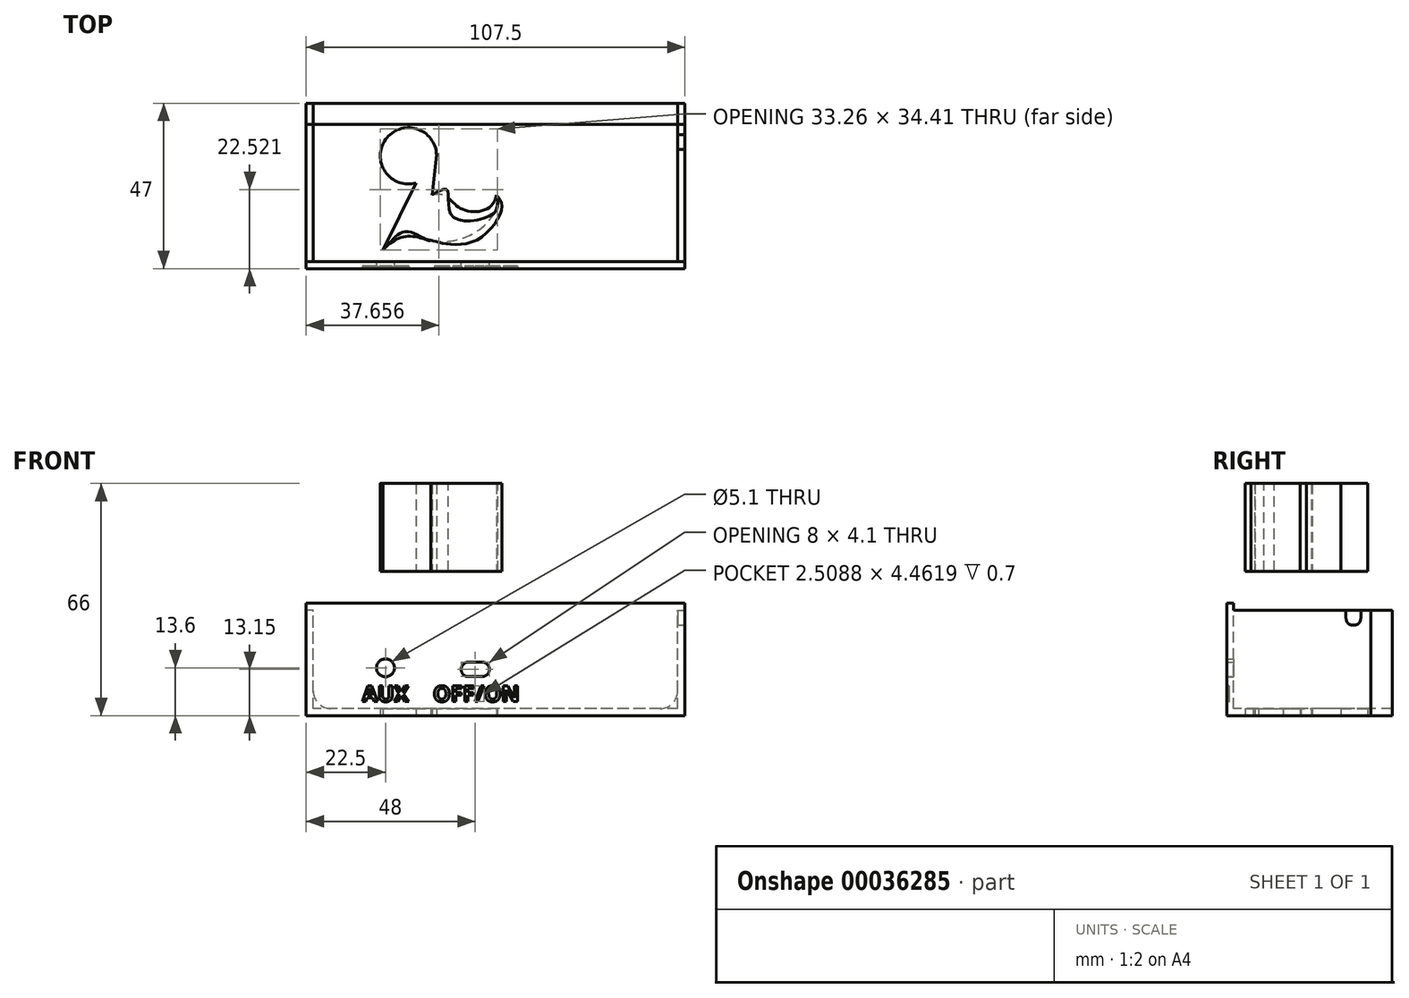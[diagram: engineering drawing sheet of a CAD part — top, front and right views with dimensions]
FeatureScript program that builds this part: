
annotation { "Feature Type Name" : "Feature", "Feature Type Description" : "" }
export const myFeature = defineFeature(function(context is Context, id is Id, definition is map)
    precondition{}
    {
        {
            var Q0;
            Q0=qCreatedBy(makeId("Top.planeOp"),FACE);
            var sketch = newSketch(context, id + "F0", { "sketchPlane" : qUnion([Q0])});
            skLineSegment(sketch, "E0.bottom", {"start": v(107.5, -32) * mm, "end": v(0, -32) * mm});
            skLineSegment(sketch, "E0.top", {"start": v(107.5, 0) * mm, "end": v(0, 0) * mm});
            skLineSegment(sketch, "E0.left", {"start": v(107.5, -32) * mm, "end": v(107.5, 0) * mm});
            skLineSegment(sketch, "E1", {"start": v(0, -32) * mm, "end": v(0, 0) * mm});
            skPoint(sketch, "E0.right.end.orphan", {"position": v(-106.05, 0) * mm});
            skSolve(sketch);
        }
        {
            var Q0;
            Q0=makeQuery(id+"F0.imprint","IMPRINT",FACE,{"disambiguationData":[TD([[makeQuery(id+"F0.imprint","IMPRINT",EDGE,{"derivedFrom":sQuery(id+"F0.wireOp",EDGE,"E0.bottom")}),-1.0]])]});
            extrude(context, id + "F1", {"entities" : qUnion([Q0]), "oppositeDirection" : true, "depth" : 2 * mm});
        }
        {
            var Q0;
            Q0=makeQuery(id+"F1.opExtrude","CAP_FACE",FACE,{"disambiguationData":[OSD([sQuery(id+"F0.wireOp",EDGE,"E0.bottom"),sQuery(id+"F0.wireOp",EDGE,"E0.top"),sQuery(id+"F0.wireOp",EDGE,"E0.left"),sQuery(id+"F0.wireOp",EDGE,"E1")])],"isStart":false});
            var sketch = newSketch(context, id + "F2", { "sketchPlane" : qUnion([Q0])});
            skLineSegment(sketch, "E2.0", {"start": v(105.5, 30) * mm, "end": v(2, 30) * mm});
            skLineSegment(sketch, "E2.1", {"start": v(105.5, 30) * mm, "end": v(105.5, 2) * mm});
            skLineSegment(sketch, "E2.2", {"start": v(105.5, 2) * mm, "end": v(2, 2) * mm});
            skLineSegment(sketch, "E2.3", {"start": v(2, 30) * mm, "end": v(2, 2) * mm});
            skLineSegment(sketch, "E3", {"start": v(2, 2) * mm, "end": v(0, 2) * mm});
            skLineSegment(sketch, "E4", {"start": v(105.5, 2) * mm, "end": v(107.5, 2) * mm});
            skSolve(sketch);
        }
        {
            var Q0;
            Q0=makeQuery(id+"F2.imprint","IMPRINT",FACE,{"disambiguationData":[TD([[makeQuery(id+"F2.imprint","IMPRINT",EDGE,{"derivedFrom":sQuery(id+"F2.wireOp",EDGE,"E2.0")}),-1.0]])]});
            extrude(context, id + "F3", {"entities" : qUnion([Q0]), "operationType" : NewBodyOperationType.ADD, "depth" : 39 * mm});
        }
        {
            var Q0;
            {var subQ0=sQuery(id+"F0.wireOp",EDGE,"E0.bottom");Q0=makeQuery(id+"F3.boolean.opBoolean","MERGE",FACE,{"derivedFrom":[makeQuery(id+"F1.opExtrude","SWEPT_FACE",FACE,{"disambiguationData":[OSD([subQ0])]}),makeQuery(id+"F3.opExtrude","SWEPT_FACE",FACE,{"disambiguationData":[OSD([subQ0])]})]});}
            var sketch = newSketch(context, id + "F4", { "sketchPlane" : qUnion([Q0])});
            skArc(sketch, "E5", {"start": v(31.19, -24.36) * mm, "mid": v(22.54, -36.75) * mm, "end": v(37.02, -32.4) * mm});
            skLineSegment(sketch, "E6", {"start": v(35.74, -20.94) * mm, "end": v(37.02, -32.4) * mm});
            skLineSegment(sketch, "E7", {"start": v(31.19, -24.36) * mm, "end": v(21.74, -5.32) * mm});
            skFitSpline(sketch, "E8", {"points": [v(35.39, -8.1) * mm, v(48.03, -10.36) * mm, v(54, -20.94) * mm], "startDerivative": vector(20.74, 5.18) * mm, "endDerivative": vector(-9.53, -21.5) * mm});
            skFitSpline(sketch, "E9", {"points": [v(21.74, -5.32) * mm, v(29.02, -9.2) * mm, v(35.39, -8.1) * mm], "startDerivative": vector(11.68, -12.14) * mm, "endDerivative": vector(6.82, 0.29) * mm});
            skFitSpline(sketch, "E10", {"points": [v(35.74, -20.94) * mm, v(43.74, -17.18) * mm, v(54, -20.94) * mm], "startDerivative": vector(27.47, -8.8) * mm, "endDerivative": vector(3.96, -29.24) * mm});
            skSolve(sketch);
        }
        {
            var Q0;
            Q0=qSketchRegion(id+"F4",true);
            extrude(context, id + "F5", {"entities" : qUnion([Q0]), "operationType" : NewBodyOperationType.REMOVE, "endBound" : BoundingType.THROUGH_ALL, "oppositeDirection" : true, "depth" : 25 * mm});
        }
        {
            var Q0;
            Q0=makeQuery(id+"F1.opExtrude","SWEPT_BODY",BODY,{"disambiguationData":[OSD([sQuery(id+"F0.wireOp",EDGE,"E0.bottom"),sQuery(id+"F0.wireOp",EDGE,"E0.top"),sQuery(id+"F0.wireOp",EDGE,"E0.left"),sQuery(id+"F0.wireOp",EDGE,"E1")])]});
            var Q1;
            Q1=makeQuery(id+"F3.opExtrude","CAP_EDGE",EDGE,{"disambiguationData":[OSD([sQuery(id+"F0.wireOp",EDGE,"E0.bottom")])],"isStart":false});
            transform(context, id + "F6", {"entities" : qUnion([Q0]), "transformType" : TransformType.ROTATION, "transformAxis" : qUnion([Q1]), "angle" : 90 * degree, "oppositeDirection" : true, "makeCopy" : false});
        }
        {
            var Q0;
            Q0=makeQuery(id+"F3.opExtrude","CAP_FACE",FACE,{"disambiguationData":[OSD([sQuery(id+"F0.wireOp",EDGE,"E0.bottom"),sQuery(id+"F0.wireOp",EDGE,"E0.left"),sQuery(id+"F0.wireOp",EDGE,"E1"),sQuery(id+"F2.wireOp",EDGE,"E2.0"),sQuery(id+"F2.wireOp",EDGE,"E2.1"),sQuery(id+"F2.wireOp",EDGE,"E2.3"),sQuery(id+"F2.wireOp",EDGE,"E3"),sQuery(id+"F2.wireOp",EDGE,"E4")])],"isStart":false});
            extrude(context, id + "F7", {"entities" : qUnion([Q0]), "depth" : 6 * mm});
        }
        {
            var Q0;
            Q0=makeQuery(id+"F3.opExtrude","CAP_EDGE",EDGE,{"disambiguationData":[OSD([sQuery(id+"F2.wireOp",EDGE,"E2.0")])],"isStart":true});
            var Q1;
            Q1=makeQuery(id+"F3.opExtrude","SWEPT_EDGE",EDGE,{"disambiguationData":[OSD([sQuery(id+"F2.wireOp",EDGE,"E2.0"),sQuery(id+"F2.wireOp",EDGE,"E2.3")])]});
            var Q2;
            Q2=makeQuery(id+"F3.opExtrude","SWEPT_EDGE",EDGE,{"disambiguationData":[OSD([sQuery(id+"F2.wireOp",EDGE,"E2.0"),sQuery(id+"F2.wireOp",EDGE,"E2.1")])]});
            fillet(context, id + "F8", {"entities" : qUnion([Q0, Q1, Q2]), "radius" : 5 * mm, "tangentPropagation" : true, "allowEdgeOverflow" : false});
        }
        {
            var Q0;
            Q0=makeQuery(id+"F1.opExtrude","CAP_FACE",FACE,{"disambiguationData":[OSD([sQuery(id+"F0.wireOp",EDGE,"E0.bottom"),sQuery(id+"F0.wireOp",EDGE,"E0.top"),sQuery(id+"F0.wireOp",EDGE,"E0.left"),sQuery(id+"F0.wireOp",EDGE,"E1")])],"isStart":false});
            var sketch = newSketch(context, id + "F9", { "sketchPlane" : qUnion([Q0])});
            skCircle(sketch, "E11", {"center": v(-22.5, -27.4) * mm, "radius": 2.55 * mm});
            skLineSegment(sketch, "E12.bottom", {"start": v(-46, -29.9) * mm, "end": v(-50, -29.9) * mm});
            skLineSegment(sketch, "E12.top", {"start": v(-46, -25.8) * mm, "end": v(-50, -25.8) * mm});
            skLineSegment(sketch, "E12.left", {"start": v(-44, -27.9) * mm, "end": v(-44, -27.8) * mm});
            skLineSegment(sketch, "E12.right", {"start": v(-52, -27.9) * mm, "end": v(-52, -27.8) * mm});
            skPoint(sketch, "E13.visualSharp", {"position": v(-44, -25.8) * mm});
            skArc(sketch, "E13.filletArc", {"start": v(-44, -27.8) * mm, "mid": v(-44.59, -26.39) * mm, "end": v(-46, -25.8) * mm});
            skPoint(sketch, "E14.visualSharp", {"position": v(-44, -29.9) * mm});
            skArc(sketch, "E14.filletArc", {"start": v(-46, -29.9) * mm, "mid": v(-44.59, -29.31) * mm, "end": v(-44, -27.9) * mm});
            skPoint(sketch, "E15.visualSharp", {"position": v(-52, -29.9) * mm});
            skArc(sketch, "E15.filletArc", {"start": v(-52, -27.9) * mm, "mid": v(-51.41, -29.31) * mm, "end": v(-50, -29.9) * mm});
            skPoint(sketch, "E16.visualSharp", {"position": v(-52, -25.8) * mm});
            skArc(sketch, "E16.filletArc", {"start": v(-50, -25.8) * mm, "mid": v(-51.41, -26.39) * mm, "end": v(-52, -27.8) * mm});
            skLineSegment(sketch, "E17", {"start": v(-48, -29.9) * mm, "end": v(-48, -25.8) * mm, "construction": true});
            skLineSegment(sketch, "E18", {"start": v(-48, -29.9) * mm, "end": v(-48, -32.37) * mm});
            skSolve(sketch);
        }
        {
            var Q0;
            Q0=makeQuery(id+"F9.imprint","IMPRINT",FACE,{"disambiguationData":[TD([[makeQuery(id+"F9.imprint","IMPRINT",EDGE,{"derivedFrom":sQuery(id+"F9.wireOp",EDGE,"E12.bottom")}),-1.0]])]});
            var Q1;
            Q1=makeQuery(id+"F9.imprint","IMPRINT",FACE,{"disambiguationData":[TD([[makeQuery(id+"F9.imprint","IMPRINT",EDGE,{"derivedFrom":sQuery(id+"F9.wireOp",EDGE,"E11")}),1.0]])]});
            extrude(context, id + "F10", {"entities" : qUnion([Q0, Q1]), "operationType" : NewBodyOperationType.REMOVE, "endBound" : BoundingType.THROUGH_ALL, "oppositeDirection" : true, "depth" : 25 * mm});
        }
        {
            var Q0;
            Q0=makeQuery(id+"F1.opExtrude","CAP_FACE",FACE,{"disambiguationData":[OSD([sQuery(id+"F0.wireOp",EDGE,"E0.bottom"),sQuery(id+"F0.wireOp",EDGE,"E0.top"),sQuery(id+"F0.wireOp",EDGE,"E0.left"),sQuery(id+"F0.wireOp",EDGE,"E1")])],"isStart":true});
            var sketch = newSketch(context, id + "F11", { "sketchPlane" : qUnion([Q0])});
            skLineSegment(sketch, "E19", {"start": v(22.5, -27.4) * mm, "end": v(22.5, -41) * mm, "construction": true});
            skLineSegment(sketch, "E20", {"start": v(22.5, -41) * mm, "end": v(32.53, -41) * mm, "construction": true});
            skSolve(sketch);
        }
        {
            var Q0;
            {var subQ0=sQuery(id+"F0.wireOp",EDGE,"E0.bottom");Q0=makeQuery(id+"F3.boolean.opBoolean","MERGE",FACE,{"derivedFrom":[makeQuery(id+"F1.opExtrude","SWEPT_FACE",FACE,{"disambiguationData":[OSD([subQ0])]}),makeQuery(id+"F3.opExtrude","SWEPT_FACE",FACE,{"disambiguationData":[OSD([subQ0])]})]});}
            var sketch = newSketch(context, id + "F12", { "sketchPlane" : qUnion([Q0])});
            skLineSegment(sketch, "E21", {"start": v(32.56, 73) * mm, "end": v(32.56, 51.6) * mm, "construction": true});
            skSolve(sketch);
        }
        {
            var Q0;
            {var subQ0=sQuery(id+"F0.wireOp",EDGE,"E0.bottom");Q0=makeQuery(id+"F11.imprint","IMPRINT",FACE,{"disambiguationData":[TD([[makeQuery(id+"F11.imprint","IMPRINT",EDGE,{"derivedFrom":makeQuery(id+"F1.opExtrude","CAP_EDGE",EDGE,{"disambiguationData":[OSD([subQ0])],"isStart":true})}),-1.0]])]});}
            var sketch = newSketch(context, id + "F14", { "sketchPlane" : qUnion([Q0])});
            skText(sketch, "E22", { "text": "AUX", "fontName": "OpenSans-Bold.ttf"});
            skText(sketch, "E23", { "text": "OFF/ON", "fontName": "OpenSans-Bold.ttf"});
            const initialGuessF14  = {"E22": [0.0159, -0.037, 1, 0, 0.0045], "E23": [0.03604, -0.037, 1, 0, 0.0045]};
            skSetInitialGuess(sketch, initialGuessF14);
            skSolve(sketch);
        }
        {
            var Q0;
            Q0=qSketchRegion(id+"F14",true);
            extrude(context, id + "F15", {"entities" : qUnion([Q0]), "operationType" : NewBodyOperationType.REMOVE, "oppositeDirection" : true, "depth" : 0.7 * mm});
        }
        {
            var Q0;
            {var subQ0=sQuery(id+"F0.wireOp",EDGE,"E0.left");Q0=makeQuery(id+"F3.boolean.opBoolean","MERGE",FACE,{"derivedFrom":[makeQuery(id+"F1.opExtrude","SWEPT_FACE",FACE,{"disambiguationData":[OSD([subQ0])]}),makeQuery(id+"F3.opExtrude","SWEPT_FACE",FACE,{"disambiguationData":[OSD([subQ0])]})]});}
            var sketch = newSketch(context, id + "F16", { "sketchPlane" : qUnion([Q0])});
            skLineSegment(sketch, "E24", {"start": v(-34.9, -11) * mm, "end": v(-34.9, -13.3) * mm});
            skLineSegment(sketch, "E25", {"start": v(-36.9, -15.3) * mm, "end": v(-37.1, -15.3) * mm});
            skLineSegment(sketch, "E26", {"start": v(-39.1, -13.3) * mm, "end": v(-39.1, -11) * mm});
            skLineSegment(sketch, "E27", {"start": v(-37, -15.3) * mm, "end": v(-37, -19.69) * mm, "construction": true});
            skPoint(sketch, "E28.visualSharp", {"position": v(-39.1, -15.3) * mm});
            skArc(sketch, "E28.filletArc", {"start": v(-39.1, -13.3) * mm, "mid": v(-38.51, -14.71) * mm, "end": v(-37.1, -15.3) * mm});
            skPoint(sketch, "E29.visualSharp", {"position": v(-34.9, -15.3) * mm});
            skArc(sketch, "E29.filletArc", {"start": v(-36.9, -15.3) * mm, "mid": v(-35.49, -14.71) * mm, "end": v(-34.9, -13.3) * mm});
            skSolve(sketch);
        }
        {
            var Q0;
            {var subQ2=sQuery(id+"F16.wireOp",EDGE,"E24");Q0=makeQuery(id+"F16.imprint","IMPRINT",FACE,{"disambiguationData":[TD([[makeQuery(id+"F16.imprint","IMPRINT",EDGE,{"derivedFrom":subQ2}),-1.0]])]});}
            extrude(context, id + "F17", {"entities" : qUnion([Q0]), "operationType" : NewBodyOperationType.REMOVE, "endBound" : BoundingType.UP_TO_NEXT, "oppositeDirection" : true, "depth" : 25 * mm});
        }
        {
            var Q0;
            Q0=qCreatedBy(makeId("Top.planeOp"),FACE);
            var sketch = newSketch(context, id + "F18", { "sketchPlane" : qUnion([Q0])});
            skLineSegment(sketch, "E30.0.0", {"start": v(21.74, -67.68) * mm, "end": v(31.19, -48.64) * mm});
            skArc(sketch, "E30.0.1", {"start": v(31.19, -48.64) * mm, "mid": v(22.54, -36.25) * mm, "end": v(37.02, -40.6) * mm});
            skLineSegment(sketch, "E30.0.2", {"start": v(37.02, -40.6) * mm, "end": v(35.74, -52.06) * mm});
            skFitSpline(sketch, "E30.0.3", {"points": [v(35.74, -52.06) * mm, v(40.08, -50.67) * mm, v(41.48, -58.07) * mm, v(53.3, -57.19) * mm, v(54, -52.06) * mm]});
            skFitSpline(sketch, "E30.0.4", {"points": [v(54, -52.06) * mm, v(55.56, -55.6) * mm, v(48.6, -64.73) * mm, v(38.9, -65.78) * mm, v(35.39, -64.9) * mm]});
            skFitSpline(sketch, "E30.0.5", {"points": [v(35.39, -64.9) * mm, v(34.32, -64.86) * mm, v(28.34, -62.42) * mm, v(23.8, -65.53) * mm, v(21.74, -67.68) * mm]});
            skSolve(sketch);
        }
        {
            var Q0;
            Q0=makeQuery(id+"F18.imprint","IMPRINT",FACE,{"disambiguationData":[TD([[makeQuery(id+"F18.imprint","IMPRINT",EDGE,{"derivedFrom":sQuery(id+"F18.wireOp",EDGE,"E30.0.0")}),-1.0]])]});
            extrude(context, id + "F19", {"entities" : qUnion([Q0]), "depth" : 25 * mm});
        }
    });
